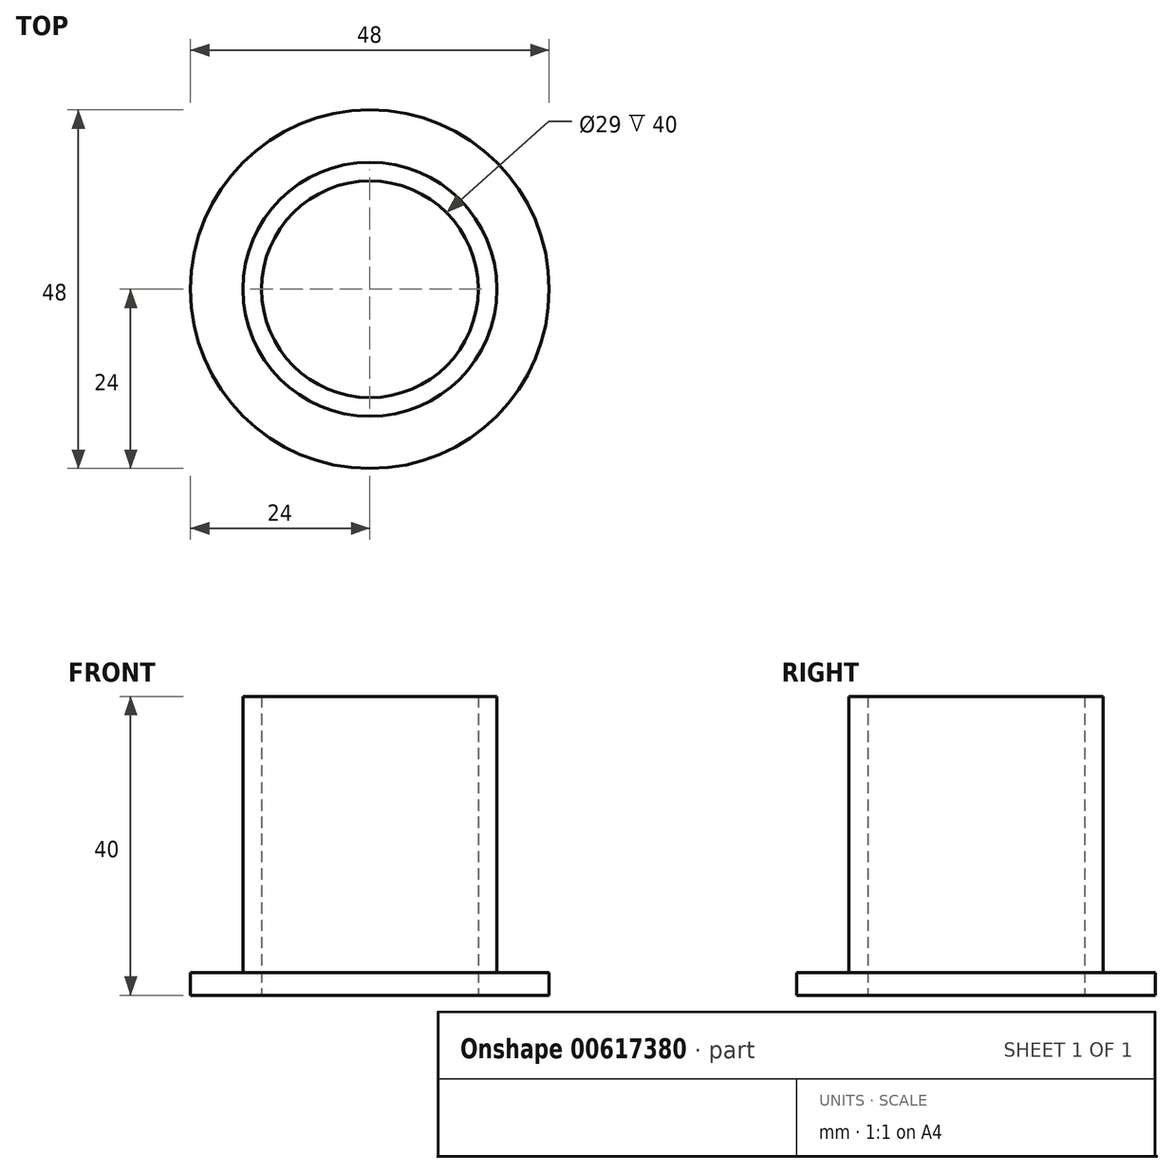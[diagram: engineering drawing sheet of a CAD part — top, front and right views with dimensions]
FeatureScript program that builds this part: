
annotation { "Feature Type Name" : "Feature", "Feature Type Description" : "" }
export const myFeature = defineFeature(function(context is Context, id is Id, definition is map)
    precondition{}
    {
        {
            var Q0;
            Q0=qCreatedBy(makeId("Top.planeOp"),FACE);
            var sketch = newSketch(context, id + "F0", { "sketchPlane" : qUnion([Q0])});
            skCircle(sketch, "E0", {"center": v(0, 0) * mm, "radius": 24 * mm});
            skCircle(sketch, "E1", {"center": v(0, 0) * mm, "radius": 14.5 * mm});
            skSolve(sketch);
        }
        {
            var Q0;
            Q0 = qSketchRegion(id + "F0", true);
            extrude(context, id + "F1", {"entities" : qUnion([Q0]), "depth" : 3 * mm, "offsetDistance" : 25.4 * mm});
        }
        {
            var Q0;
            Q0=qCreatedBy(makeId("Top.planeOp"),FACE);
            var sketch = newSketch(context, id + "F2", { "sketchPlane" : qUnion([Q0])});
            skCircle(sketch, "E2", {"center": v(0, 0) * mm, "radius": 17 * mm});
            skCircle(sketch, "E3", {"center": v(0, 0) * mm, "radius": 0.68 * mm});
            skCircle(sketch, "E4", {"center": v(0, 0) * mm, "radius": 14.5 * mm});
            skSolve(sketch);
        }
        {
            var Q0;
            Q0 = qSketchRegion(id + "F2", true);
            extrude(context, id + "F3", {"entities" : qUnion([Q0]), "operationType" : NewBodyOperationType.ADD, "depth" : 40 * mm, "offsetDistance" : 25 * mm});
        }
    });
